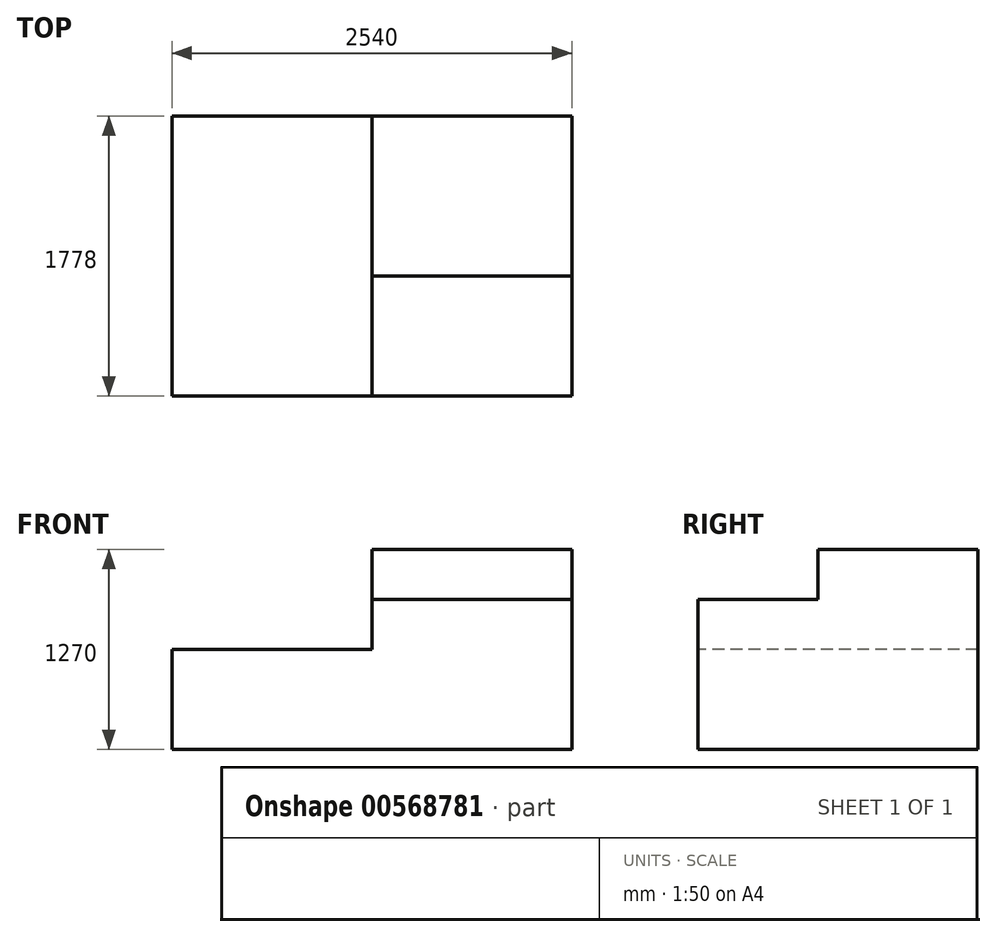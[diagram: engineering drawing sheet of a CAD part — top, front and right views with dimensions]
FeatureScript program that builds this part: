
annotation { "Feature Type Name" : "Feature", "Feature Type Description" : "" }
export const myFeature = defineFeature(function(context is Context, id is Id, definition is map)
    precondition{}
    {
        {
            var Q0;
            Q0=qCreatedBy(makeId("Front.planeOp"),FACE);
            var sketch = newSketch(context, id + "F0", { "sketchPlane" : qUnion([Q0])});
            skLineSegment(sketch, "E0.bottom", {"start": v(-2431.77, 1217.74) * mm, "end": v(108.23, 1217.74) * mm});
            skLineSegment(sketch, "E0.top", {"start": v(-2431.77, -52.26) * mm, "end": v(108.23, -52.26) * mm});
            skLineSegment(sketch, "E0.left", {"start": v(-2431.77, 1217.74) * mm, "end": v(-2431.77, -52.26) * mm});
            skLineSegment(sketch, "E0.right", {"start": v(108.23, 1217.74) * mm, "end": v(108.23, -52.26) * mm});
            skSolve(sketch);
        }
        {
            var Q0;
            Q0 = qSketchRegion(id + "F0", true);
            extrude(context, id + "F1", {"entities" : qUnion([Q0]), "depth" : 1778 * mm, "offsetDistance" : 25.4 * mm});
        }
        {
            var Q0;
            Q0=makeQuery(id+"F1.opExtrude","CAP_FACE",FACE,{"disambiguationData":[OSD([sQuery(id+"F0.wireOp",EDGE,"E0.bottom"),sQuery(id+"F0.wireOp",EDGE,"E0.top"),sQuery(id+"F0.wireOp",EDGE,"E0.left"),sQuery(id+"F0.wireOp",EDGE,"E0.right")])],"isStart":false});
            var sketch = newSketch(context, id + "F2", { "sketchPlane" : qUnion([Q0])});
            skLineSegment(sketch, "E1.bottom", {"start": v(-2431.77, 1217.74) * mm, "end": v(-1161.77, 1217.74) * mm});
            skLineSegment(sketch, "E1.top", {"start": v(-2431.77, 582.74) * mm, "end": v(-1161.77, 582.74) * mm});
            skLineSegment(sketch, "E1.left", {"start": v(-2431.77, 1217.74) * mm, "end": v(-2431.77, 582.74) * mm});
            skLineSegment(sketch, "E1.right", {"start": v(-1161.77, 1217.74) * mm, "end": v(-1161.77, 582.74) * mm});
            skSolve(sketch);
        }
        {
            var Q0;
            Q0 = qSketchRegion(id + "F2", true);
            extrude(context, id + "F3", {"entities" : qUnion([Q0]), "operationType" : NewBodyOperationType.REMOVE, "endBound" : BoundingType.THROUGH_ALL, "oppositeDirection" : true, "depth" : 25.4 * mm, "offsetDistance" : 25.4 * mm});
        }
        {
            var Q0;
            Q0=makeQuery(id+"F3.boolean.opBoolean","COPY",FACE,{"derivedFrom":makeQuery(id+"F3.opExtrude","SWEPT_FACE",FACE,{"disambiguationData":[OSD([sQuery(id+"F2.wireOp",EDGE,"E1.right")])]})});
            var sketch = newSketch(context, id + "F4", { "sketchPlane" : qUnion([Q0])});
            skPoint(sketch, "E2.oppositeSnap0", {"position": v(1778, 900.24) * mm});
            skLineSegment(sketch, "E2.bottom", {"start": v(1778, 1217.74) * mm, "end": v(1016, 1217.74) * mm});
            skLineSegment(sketch, "E2.top", {"start": v(1778, 900.24) * mm, "end": v(1016, 900.24) * mm});
            skLineSegment(sketch, "E2.left", {"start": v(1778, 1217.74) * mm, "end": v(1778, 900.24) * mm});
            skLineSegment(sketch, "E2.right", {"start": v(1016, 1217.74) * mm, "end": v(1016, 900.24) * mm});
            skSolve(sketch);
        }
        {
            var Q0;
            Q0=makeQuery(id+"F4.imprint","IMPRINT",FACE,{"disambiguationData":[TD([[makeQuery(id+"F4.imprint","IMPRINT",EDGE,{"derivedFrom":sQuery(id+"F4.wireOp",EDGE,"E2.bottom")}),-1.0]])]});
            extrude(context, id + "F5", {"entities" : qUnion([Q0]), "operationType" : NewBodyOperationType.REMOVE, "endBound" : BoundingType.THROUGH_ALL, "oppositeDirection" : true, "depth" : 25.4 * mm, "offsetDistance" : 25.4 * mm});
        }
    });
